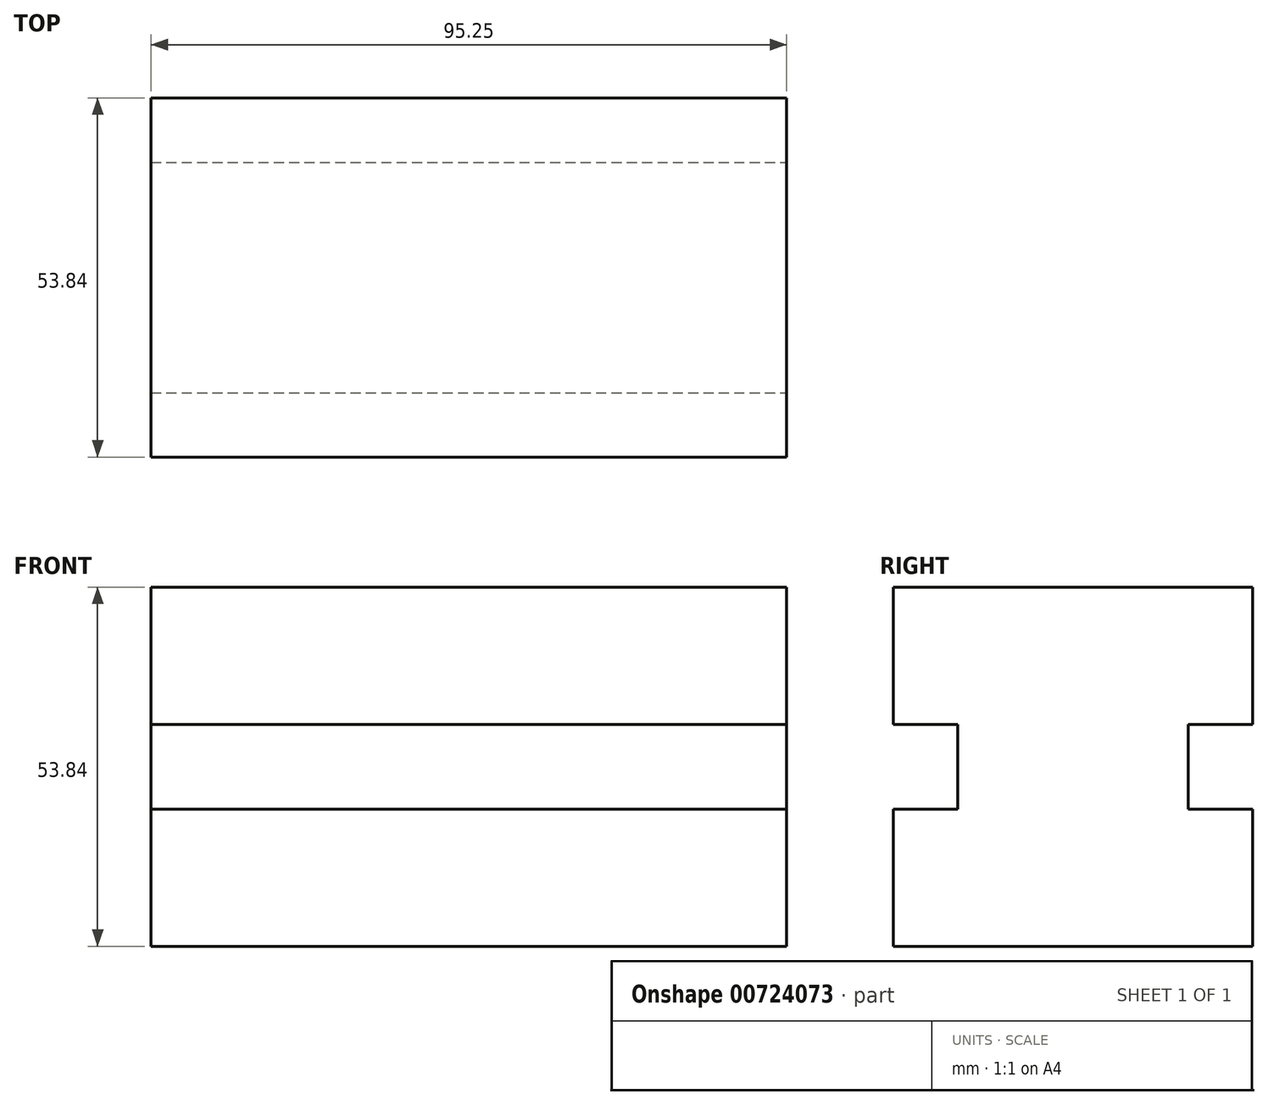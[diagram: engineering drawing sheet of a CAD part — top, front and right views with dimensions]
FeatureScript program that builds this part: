
annotation { "Feature Type Name" : "Feature", "Feature Type Description" : "" }
export const myFeature = defineFeature(function(context is Context, id is Id, definition is map)
    precondition{}
    {
        {
            var Q0;
            Q0=qCreatedBy(makeId("Right.planeOp"),FACE);
            var sketch = newSketch(context, id + "F0", { "sketchPlane" : qUnion([Q0])});
            skLineSegment(sketch, "E0.bottom", {"start": v(-26.92, 26.92) * mm, "end": v(26.92, 26.92) * mm});
            skLineSegment(sketch, "E0.top", {"start": v(-26.92, -26.92) * mm, "end": v(26.92, -26.92) * mm});
            skLineSegment(sketch, "E0.left", {"start": v(-26.92, 26.92) * mm, "end": v(-26.92, 6.35) * mm});
            skLineSegment(sketch, "E0.right", {"start": v(26.92, 26.92) * mm, "end": v(26.92, 6.35) * mm});
            skPoint(sketch, "E0.middle", {"position": v(0, 0) * mm});
            skLineSegment(sketch, "E1.bottom", {"start": v(-26.92, 6.35) * mm, "end": v(-17.27, 6.35) * mm});
            skLineSegment(sketch, "E2", {"start": v(-17.27, 6.35) * mm, "end": v(-17.27, -6.35) * mm});
            skLineSegment(sketch, "E3", {"start": v(-17.27, -6.35) * mm, "end": v(-26.92, -6.35) * mm});
            skLineSegment(sketch, "E4.trimOffspring", {"start": v(-26.92, -6.35) * mm, "end": v(-26.92, -26.92) * mm});
            skLineSegment(sketch, "E5", {"start": v(0, 33.14) * mm, "end": v(0, -39.2) * mm, "construction": true});
            skPoint(sketch, "E5.startSnap0", {"position": v(0, 26.92) * mm});
            skLineSegment(sketch, "E6.MirrorCS", {"start": v(26.92, 6.35) * mm, "end": v(17.27, 6.35) * mm});
            skLineSegment(sketch, "E7.MirrorCS", {"start": v(17.27, 6.35) * mm, "end": v(17.27, -6.35) * mm});
            skLineSegment(sketch, "E8.MirrorCS", {"start": v(17.27, -6.35) * mm, "end": v(26.92, -6.35) * mm});
            skLineSegment(sketch, "E9.trimOffspring", {"start": v(26.92, -6.35) * mm, "end": v(26.92, -26.92) * mm});
            skSolve(sketch);
        }
        {
            var Q0;
            Q0=makeQuery(id+"F0.imprint","IMPRINT",FACE,{"disambiguationData":[TD([[makeQuery(id+"F0.imprint","IMPRINT",EDGE,{"derivedFrom":sQuery(id+"F0.wireOp",EDGE,"E0.bottom")}),-1.0]])]});
            extrude(context, id + "F1", {"entities" : qUnion([Q0]), "oppositeDirection" : true, "depth" : 95.25 * mm, "offsetDistance" : 25.4 * mm});
        }
    });
